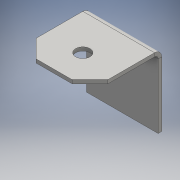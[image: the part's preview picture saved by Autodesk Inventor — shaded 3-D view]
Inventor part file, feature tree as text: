
AUTODESK INVENTOR PART (.ipt)
format: ipt  version: 2016 (Build 200138000, 138)  size: 119,808 bytes
history: native  units: mm
features: sheet_metal_op x4, sketch x3, other x3, hole x1
ambient origin geometry x8: Origin, YZ Plane, XZ Plane, XY Plane, X Axis, Y Axis, Z Axis, Center Point
bodies: Solid1 (feature_tree)
feature tree (11):
  sheet_metal_op  "Face1"
  sheet_metal_op  "Flange1"
  sketch  "Sketch3"  dims[d3=1.0mm d4=0.5mm d5=2.0mm d6=1.0mm d7=20.0mm d8=90.0deg d9=1.0mm d10=4.0mm d11=1.0mm d12=1.0mm d13=5.0mm d14=6.0mm d15=45.0deg d16=4.0mm d17=6.0mm d18=4.0mm d19=2.0mm d20=90.0deg d21=1.0mm d22=20.594885mm d23=8.0mm]
  other  "Corner Chamfer1"
  hole  "Hole1"  [1 undecoded]
  sketch  "Sketch1"  dims[d0=20.0mm d1=20.0mm]
  other  "Plate1"
  sketch  "Sketch2"  dims[d2=1.0mm]
  other  "Plate2"
  sheet_metal_op  "Bend1"
  sheet_metal_op  "Corner1"
note: 1 required parameter value undecoded (feature->parameter linkage not recoverable at this tier; creation-order binding heuristic only, values carry confidence <= 0.55)
